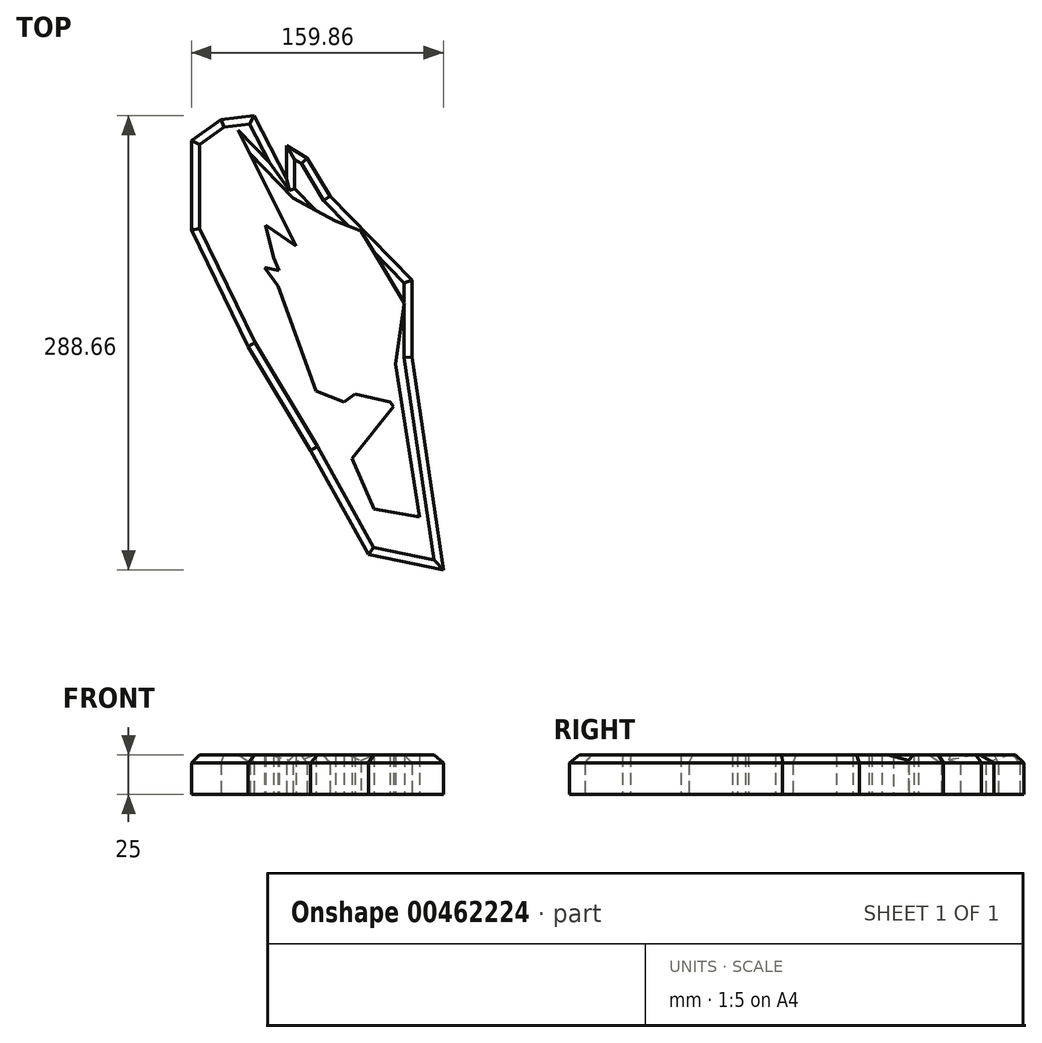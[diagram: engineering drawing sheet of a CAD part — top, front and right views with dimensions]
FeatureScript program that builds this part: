
annotation { "Feature Type Name" : "Feature", "Feature Type Description" : "" }
export const myFeature = defineFeature(function(context is Context, id is Id, definition is map)
    precondition{}
    {
        {
            var Q0;
            Q0=qCreatedBy(makeId("Top.planeOp"),FACE);
            var sketch = newSketch(context, id + "F0", { "sketchPlane" : qUnion([Q0])});
            skLineSegment(sketch, "E0", {"start": v(-7.04, -71.6) * mm, "end": v(-42.57, 27.1) * mm});
            skLineSegment(sketch, "E1", {"start": v(-45.3, 43.99) * mm, "end": v(36.91, -66.49) * mm});
            skLineSegment(sketch, "E2", {"start": v(36.91, -66.49) * mm, "end": v(10.4, -99.37) * mm});
            skLineSegment(sketch, "E3", {"start": v(10.4, -99.37) * mm, "end": v(24.27, -131.4) * mm});
            skLineSegment(sketch, "E4", {"start": v(24.27, -131.4) * mm, "end": v(53.21, -136.59) * mm});
            skLineSegment(sketch, "E5", {"start": v(53.21, -136.59) * mm, "end": v(30.39, 10.44) * mm});
            skLineSegment(sketch, "E6", {"start": v(30.39, 10.44) * mm, "end": v(30.39, -50.53) * mm});
            skLineSegment(sketch, "E7", {"start": v(30.39, -50.53) * mm, "end": v(16.06, 5.66) * mm});
            skLineSegment(sketch, "E8", {"start": v(16.06, 5.66) * mm, "end": v(0, -39.6) * mm});
            skLineSegment(sketch, "E9", {"start": v(0, -39.6) * mm, "end": v(0, -34.77) * mm});
            skLineSegment(sketch, "E10", {"start": v(0, -34.77) * mm, "end": v(-15.87, -13.78) * mm});
            skLineSegment(sketch, "E11", {"start": v(-15.87, -13.78) * mm, "end": v(-16.46, -12.71) * mm});
            skLineSegment(sketch, "E12", {"start": v(-31.01, 13.03) * mm, "end": v(-24.78, 13.35) * mm});
            skLineSegment(sketch, "E13", {"start": v(-13.34, 10.86) * mm, "end": v(-21.85, -6.22) * mm});
            skLineSegment(sketch, "E14", {"start": v(-21.85, -6.22) * mm, "end": v(-19.14, -13.78) * mm});
            skLineSegment(sketch, "E15", {"start": v(-19.14, -13.78) * mm, "end": v(-16.46, -12.71) * mm});
            skLineSegment(sketch, "E16", {"start": v(-15.87, -12.71) * mm, "end": v(-2.4, 16.8) * mm});
            skLineSegment(sketch, "E17", {"start": v(-2.4, 16.8) * mm, "end": v(21.24, -7.14) * mm});
            skLineSegment(sketch, "E18", {"start": v(21.24, -7.14) * mm, "end": v(8.45, 29.59) * mm});
            skLineSegment(sketch, "E19", {"start": v(8.45, 29.59) * mm, "end": v(30.39, -20.04) * mm});
            skLineSegment(sketch, "E20", {"start": v(30.39, -20.04) * mm, "end": v(30.39, 5.66) * mm});
            skLineSegment(sketch, "E21", {"start": v(30.39, 5.66) * mm, "end": v(16.06, 37.27) * mm});
            skLineSegment(sketch, "E22", {"start": v(16.06, 37.27) * mm, "end": v(-19.18, 45.78) * mm});
            skLineSegment(sketch, "E23", {"start": v(-19.18, 45.78) * mm, "end": v(-5.9, 19.03) * mm});
            skLineSegment(sketch, "E24", {"start": v(-5.9, 19.03) * mm, "end": v(6.32, -6.64) * mm});
            skLineSegment(sketch, "E25", {"start": v(6.32, -6.64) * mm, "end": v(-7.62, -6.64) * mm});
            skLineSegment(sketch, "E26", {"start": v(-7.62, -6.64) * mm, "end": v(-18.78, 15.78) * mm});
            skLineSegment(sketch, "E27", {"start": v(-18.78, 15.78) * mm, "end": v(-23.54, 34.46) * mm});
            skLineSegment(sketch, "E28", {"start": v(-23.54, 34.46) * mm, "end": v(-44.62, 48.74) * mm});
            skLineSegment(sketch, "E29", {"start": v(-44.62, 48.74) * mm, "end": v(-41.17, 35.22) * mm});
            skLineSegment(sketch, "E30", {"start": v(-41.17, 35.22) * mm, "end": v(-39.41, 28.33) * mm});
            skLineSegment(sketch, "E31", {"start": v(-39.41, 28.33) * mm, "end": v(-35.76, 20.03) * mm});
            skLineSegment(sketch, "E32", {"start": v(-35.76, 20.03) * mm, "end": v(-45.04, 21.92) * mm});
            skLineSegment(sketch, "E33", {"start": v(-45.04, 21.92) * mm, "end": v(-19.14, -13.78) * mm});
            skLineSegment(sketch, "E34", {"start": v(-6.59, -1.47) * mm, "end": v(-54.47, 94.31) * mm});
            skLineSegment(sketch, "E35", {"start": v(-54.47, 94.31) * mm, "end": v(-27.07, 66.03) * mm});
            skLineSegment(sketch, "E36", {"start": v(-27.07, 66.03) * mm, "end": v(0, 51.46) * mm});
            skLineSegment(sketch, "E37", {"start": v(0, 51.46) * mm, "end": v(16.06, 45.09) * mm});
            skLineSegment(sketch, "E38", {"start": v(16.06, 45.09) * mm, "end": v(43.72, -0.53) * mm});
            skLineSegment(sketch, "E39", {"start": v(43.72, -0.53) * mm, "end": v(34.61, -63.4) * mm});
            skLineSegment(sketch, "E40", {"start": v(34.61, -63.4) * mm, "end": v(12.22, -58.4) * mm});
            skLineSegment(sketch, "E41", {"start": v(12.22, -58.4) * mm, "end": v(5.24, -63.6) * mm});
            skLineSegment(sketch, "E42", {"start": v(5.24, -63.6) * mm, "end": v(-27.51, -50.53) * mm});
            skLineSegment(sketch, "E43", {"start": v(-27.51, -50.53) * mm, "end": v(-35.88, -25.74) * mm});
            skLineSegment(sketch, "E44", {"start": v(-35.88, -25.74) * mm, "end": v(-63.1, 31.47) * mm});
            skLineSegment(sketch, "E45", {"start": v(-63.1, 31.47) * mm, "end": v(-63.1, 92.53) * mm});
            skLineSegment(sketch, "E46", {"start": v(-63.1, 92.53) * mm, "end": v(-72.74, 115.97) * mm});
            skLineSegment(sketch, "E47", {"start": v(-72.74, 115.97) * mm, "end": v(-51.64, 118.42) * mm});
            skLineSegment(sketch, "E48", {"start": v(-51.64, 118.42) * mm, "end": v(-31.03, 78.27) * mm});
            skLineSegment(sketch, "E49", {"start": v(-31.03, 78.27) * mm, "end": v(-31.03, 99.35) * mm});
            skLineSegment(sketch, "E50", {"start": v(-31.03, 99.35) * mm, "end": v(-18.13, 91.51) * mm});
            skLineSegment(sketch, "E51", {"start": v(-18.13, 91.51) * mm, "end": v(-3.52, 67.35) * mm});
            skLineSegment(sketch, "E52", {"start": v(-3.52, 67.35) * mm, "end": v(48.57, 14.03) * mm});
            skLineSegment(sketch, "E53", {"start": v(48.57, 14.03) * mm, "end": v(48.57, -34.9) * mm});
            skLineSegment(sketch, "E54", {"start": v(48.57, -34.9) * mm, "end": v(68.44, -170.24) * mm});
            skLineSegment(sketch, "E55", {"start": v(68.44, -170.24) * mm, "end": v(20.83, -160.22) * mm});
            skLineSegment(sketch, "E56", {"start": v(20.83, -160.22) * mm, "end": v(-15.87, -94.27) * mm});
            skLineSegment(sketch, "E57", {"start": v(-15.87, -94.27) * mm, "end": v(-55.58, -28.23) * mm});
            skLineSegment(sketch, "E58", {"start": v(-55.58, -28.23) * mm, "end": v(-91.42, 45.58) * mm});
            skLineSegment(sketch, "E59", {"start": v(-91.42, 45.58) * mm, "end": v(-91.42, 102.4) * mm});
            skLineSegment(sketch, "E60", {"start": v(-91.42, 102.4) * mm, "end": v(-72.74, 115.97) * mm});
            skSolve(sketch);
        }
        {
            var Q0;
            Q0 = qSketchRegion(id + "F0", true);
            extrude(context, id + "F1", {"entities" : qUnion([Q0]), "depth" : 25 * mm});
        }
        {
            var Q0;
            Q0=makeQuery(id+"F1.opExtrude","CAP_EDGE",EDGE,{"disambiguationData":[OSD([sQuery(id+"F0.wireOp",EDGE,"E57")])],"isStart":false});
            var Q1;
            Q1=makeQuery(id+"F1.opExtrude","CAP_EDGE",EDGE,{"disambiguationData":[OSD([sQuery(id+"F0.wireOp",EDGE,"E58")])],"isStart":false});
            var Q2;
            Q2=makeQuery(id+"F1.opExtrude","CAP_EDGE",EDGE,{"disambiguationData":[OSD([sQuery(id+"F0.wireOp",EDGE,"E56")])],"isStart":false});
            var Q3;
            Q3=makeQuery(id+"F1.opExtrude","CAP_EDGE",EDGE,{"disambiguationData":[OSD([sQuery(id+"F0.wireOp",EDGE,"E55")])],"isStart":false});
            var Q4;
            Q4=makeQuery(id+"F1.opExtrude","CAP_EDGE",EDGE,{"disambiguationData":[OSD([sQuery(id+"F0.wireOp",EDGE,"E54")])],"isStart":false});
            var Q5;
            Q5=makeQuery(id+"F1.opExtrude","CAP_EDGE",EDGE,{"disambiguationData":[OSD([sQuery(id+"F0.wireOp",EDGE,"E52")])],"isStart":false});
            var Q6;
            Q6=makeQuery(id+"F1.opExtrude","CAP_EDGE",EDGE,{"disambiguationData":[OSD([sQuery(id+"F0.wireOp",EDGE,"E53")])],"isStart":false});
            var Q7;
            Q7=makeQuery(id+"F1.opExtrude","CAP_EDGE",EDGE,{"disambiguationData":[OSD([sQuery(id+"F0.wireOp",EDGE,"E51")])],"isStart":false});
            var Q8;
            Q8=makeQuery(id+"F1.opExtrude","CAP_EDGE",EDGE,{"disambiguationData":[OSD([sQuery(id+"F0.wireOp",EDGE,"E50")])],"isStart":false});
            var Q9;
            Q9=makeQuery(id+"F1.opExtrude","CAP_EDGE",EDGE,{"disambiguationData":[OSD([sQuery(id+"F0.wireOp",EDGE,"E49")])],"isStart":false});
            var Q10;
            Q10=makeQuery(id+"F1.opExtrude","CAP_EDGE",EDGE,{"disambiguationData":[OSD([sQuery(id+"F0.wireOp",EDGE,"E48")])],"isStart":false});
            var Q11;
            Q11=makeQuery(id+"F1.opExtrude","CAP_EDGE",EDGE,{"disambiguationData":[OSD([sQuery(id+"F0.wireOp",EDGE,"E47")])],"isStart":false});
            var Q12;
            Q12=makeQuery(id+"F1.opExtrude","CAP_EDGE",EDGE,{"disambiguationData":[OSD([sQuery(id+"F0.wireOp",EDGE,"E60")])],"isStart":false});
            var Q13;
            Q13=makeQuery(id+"F1.opExtrude","CAP_EDGE",EDGE,{"disambiguationData":[OSD([sQuery(id+"F0.wireOp",EDGE,"E59")])],"isStart":false});
            var Q14;
            Q14=makeQuery(id+"F1.opExtrude","CAP_EDGE",EDGE,{"disambiguationData":[OSD([sQuery(id+"F0.wireOp",EDGE,"E35")])],"isStart":false});
            chamfer(context, id + "F2", {"entities" : qUnion([Q0, Q1, Q2, Q3, Q4, Q5, Q6, Q7, Q8, Q9, Q10, Q11, Q12, Q13, Q14]), "width" : 5 * mm, "tangentPropagation" : true});
        }
    });
